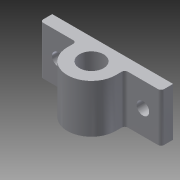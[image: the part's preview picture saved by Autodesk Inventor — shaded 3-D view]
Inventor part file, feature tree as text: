
AUTODESK INVENTOR PART (.ipt)
format: ipt  version: 2014 SP1 (Build 180222100, 222)  size: 128,512 bytes
history: native  units: in
note: dims shown in document units (in); Inventor stores cm internally (conversion verified against a paired STEP export)
features: sketch x2, extrude x2, projected_geometry x2, fillet x1
ambient origin geometry x8: Origin, YZ Plane, XZ Plane, XY Plane, X Axis, Y Axis, Z Axis, Center Point
bodies: Solid1 (feature_tree)
feature tree (7):
  sketch  "Sketch1"  dims[d0=1.0in d1=0.9375in d2=0.5in]
  extrude  "Extrusion1"  Depth=0.9375in
  fillet  "Fillet1"  Radius=0.5in
  extrude  "Extrusion3"  Depth=0.25in
  sketch  "Sketch2"  dims[d3=1.0in d4=0.0in d9=0.25in d10=0.75in d11=0.75in d12=0.25in d13=0.5in d14=0.0625in d15=0.26in d16=0.26in d17=0.25in d18=0.0in d20=0.4375in d21=1.75in]
  projected_geometry  "Projected Loop1"
  projected_geometry  "Projected Loop2"
